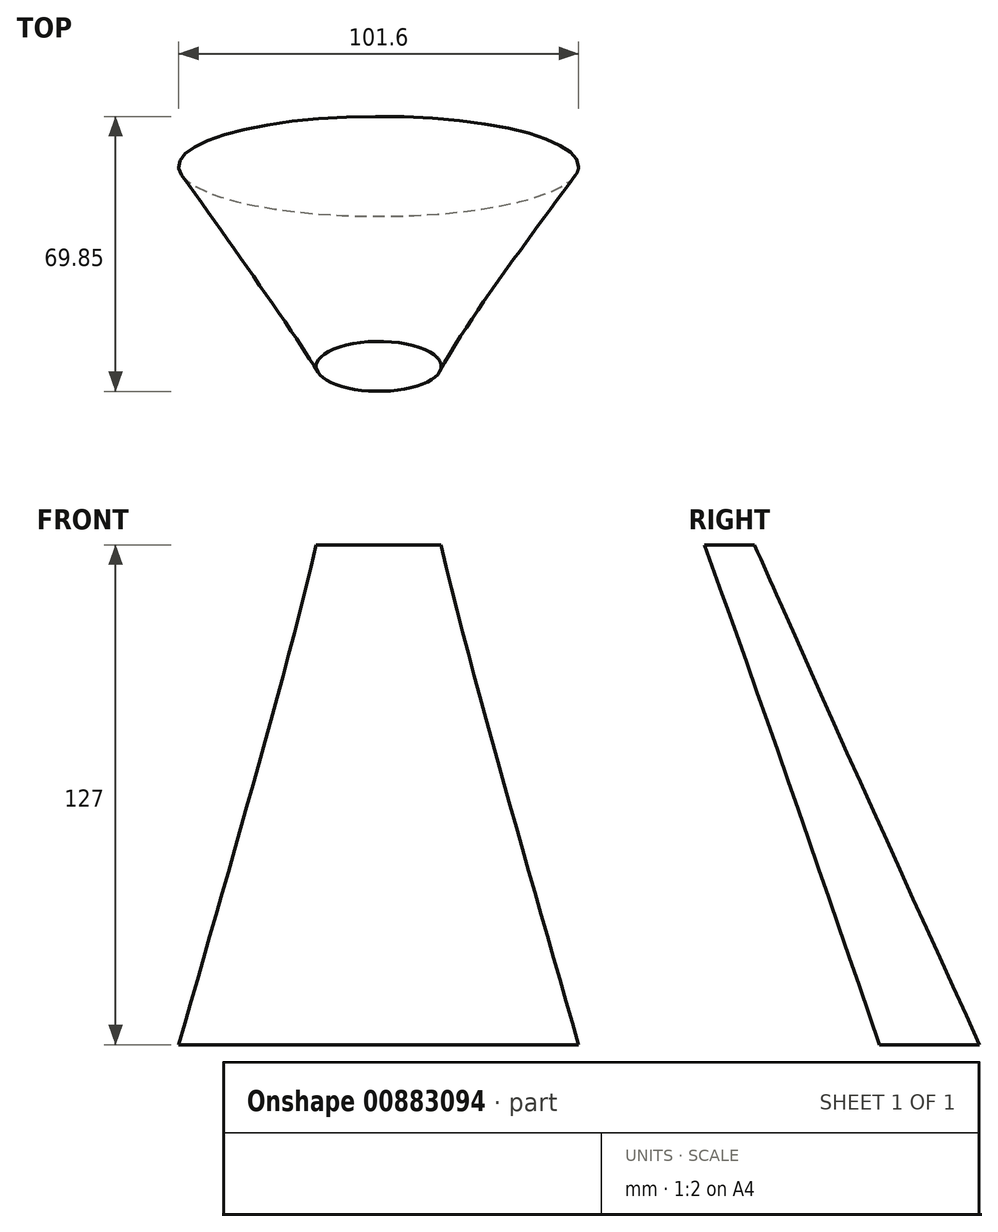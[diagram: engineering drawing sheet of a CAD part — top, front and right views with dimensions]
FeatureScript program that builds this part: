
annotation { "Feature Type Name" : "Feature", "Feature Type Description" : "" }
export const myFeature = defineFeature(function(context is Context, id is Id, definition is map)
    precondition{}
    {
        {
            var Q0;
            Q0=qCreatedBy(makeId("Top.planeOp"),FACE);
            var sketch = newSketch(context, id + "F0", { "sketchPlane" : qUnion([Q0])});
            skEllipse(sketch, "E0", {"center": v(0, 0) * mm, "majorRadius": 50.8 * mm, "minorRadius": 12.7 * mm, "majorAxis": v(1, 0)});
            skSolve(sketch);
        }
        {
            var Q0;
            Q0=qCreatedBy(makeId("Top.planeOp"),FACE);
            cPlane(context, id + "F1", {"entities" : qUnion([Q0]), "cplaneType" : CPlaneType.OFFSET, "offset" : 127 * mm, "width" : 152.4 * mm, "height" : 152.4 * mm});
        }
        {
            var Q0;
            Q0=qCreatedBy(id+"F1.planeOp",FACE);
            var sketch = newSketch(context, id + "F2", { "sketchPlane" : qUnion([Q0])});
            skEllipse(sketch, "E1", {"center": v(0, -50.8) * mm, "majorRadius": 15.88 * mm, "minorRadius": 6.35 * mm, "majorAxis": v(-1, 0)});
            skSolve(sketch);
        }
        {
            var Q0;
            Q0=makeQuery(id+"F0.imprint","IMPRINT",FACE,{"disambiguationData":[TD([[makeQuery(id+"F0.imprint","IMPRINT",EDGE,{"derivedFrom":sQuery(id+"F0.wireOp",EDGE,"E0")}),1.0]])]});
            var Q1;
            Q1=makeQuery(id+"F2.imprint","IMPRINT",FACE,{"disambiguationData":[TD([[makeQuery(id+"F2.imprint","IMPRINT",EDGE,{"derivedFrom":sQuery(id+"F2.wireOp",EDGE,"E1")}),1.0]])]});
            loft(context, id + "F3", {"sheetProfilesArray" : [{ "sheetProfileEntities" : qUnion([Q0]) }, { "sheetProfileEntities" : qUnion([Q1]) }]});
        }
    });
